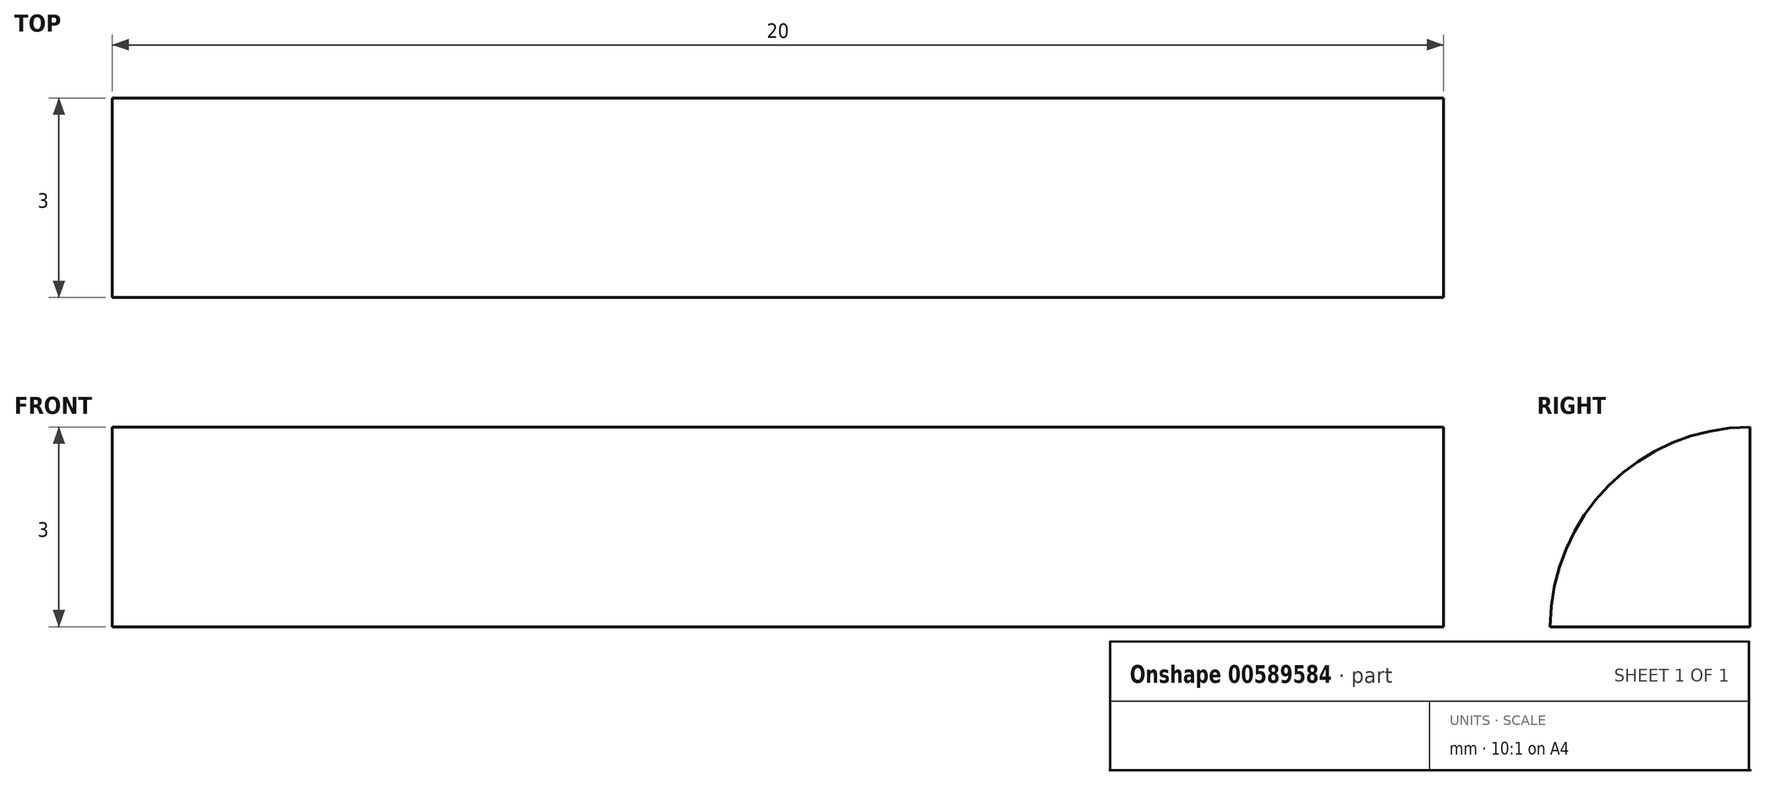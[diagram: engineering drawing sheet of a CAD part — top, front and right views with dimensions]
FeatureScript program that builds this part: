
annotation { "Feature Type Name" : "Feature", "Feature Type Description" : "" }
export const myFeature = defineFeature(function(context is Context, id is Id, definition is map)
    precondition{}
    {
        {
            var Q0;
            Q0=qCreatedBy(makeId("Front.planeOp"),FACE);
            var sketch = newSketch(context, id + "F0", { "sketchPlane" : qUnion([Q0])});
            skLineSegment(sketch, "E0", {"start": v(-23.96, 0) * mm, "end": v(26.68, 0) * mm, "construction": true});
            skLineSegment(sketch, "E1", {"start": v(0, 24.2) * mm, "end": v(0, -21.64) * mm, "construction": true});
            skLineSegment(sketch, "E2", {"start": v(-9.32, 3) * mm, "end": v(10.68, 3) * mm});
            skLineSegment(sketch, "E3", {"start": v(-9.32, 3) * mm, "end": v(-9.32, 0) * mm});
            skLineSegment(sketch, "E4", {"start": v(10.68, 3) * mm, "end": v(10.68, 0) * mm});
            skLineSegment(sketch, "E5", {"start": v(-9.32, 0) * mm, "end": v(10.68, 0) * mm});
            skSolve(sketch);
        }
        {
            var Q0;
            Q0 = qSketchRegion(id + "F0", true);
            var Q1;
            Q1=sQuery(id+"F0.wireOp",EDGE,"E5");
            revolve(context, id + "F1", {"entities" : qUnion([Q0]), "axis" : qUnion([Q1]), "revolveType" : RevolveType.ONE_DIRECTION, "angle" : 90 * degree});
        }
    });
